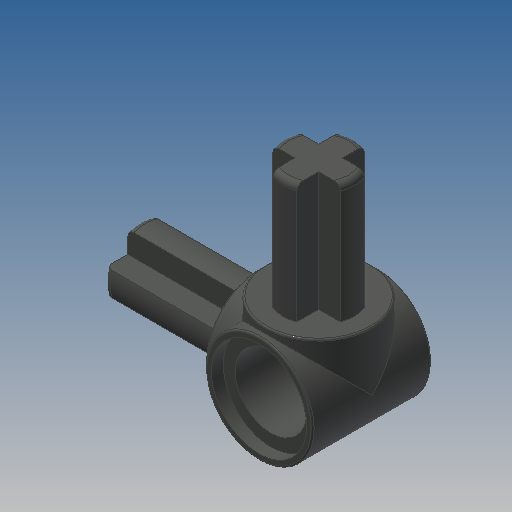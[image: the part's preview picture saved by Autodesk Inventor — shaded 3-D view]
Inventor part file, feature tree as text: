
AUTODESK INVENTOR PART (.ipt)
format: ipt  version: 2022.2 (Build 262287000, 287)  size: 260,608 bytes
history: native  units: in
note: dims shown in document units (in); Inventor stores cm internally (conversion verified against a paired STEP export)
features: extrude x4, sketch x4, mirror x1, plane x1, pattern_circular x1, fillet x1
ambient origin geometry x8: Origin, YZ Plane, XZ Plane, XY Plane, X Axis, Y Axis, Z Axis, Center Point
bodies: Solid1 (feature_tree)
feature tree (12):
  extrude  "Extrusion1"  Depth=0.2835in
  extrude  "Extrusion4"  TaperAngle=0.0deg  [1 undecoded]
  mirror  "Mirror1"
  plane  "Work Plane2"
  extrude  "Extrusion2"  Depth=0.315in
  extrude  "Extrusion3"  Depth=0.0157in
  pattern_circular  "Circular Pattern1"  [2 undecoded]
  fillet  "Fillet1"  Radius=0.315in
  sketch  "Sketch1"  dims[d0=0.189in d1=0.2835in]
  sketch  "Sketch2"  dims[d3=0.315in d4=0.0in]
  sketch  "Sketch3"  dims[d6=0.1575in d7=0.315in]
  sketch  "Sketch4"  dims[d8=0.0in d9=0.063in d10=0.189in d11=0.315in d12=0.0in d13=0.7874in d14=90.0deg d16=0.0039in d17=0.0157in d18=0.252in d19=0.0315in d20=0.0in]
note: 3 required parameter values undecoded (feature->parameter linkage not recoverable at this tier; creation-order binding heuristic only, values carry confidence <= 0.55)
